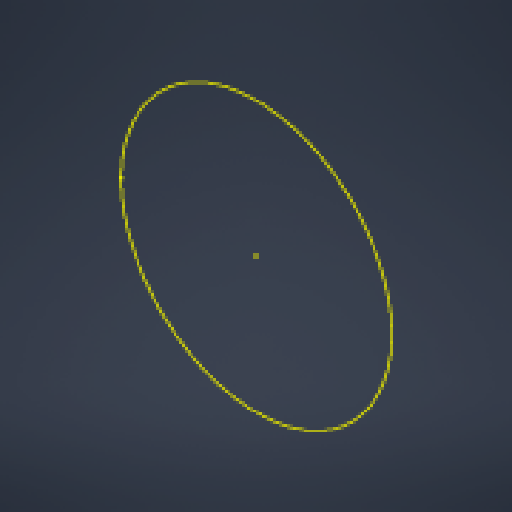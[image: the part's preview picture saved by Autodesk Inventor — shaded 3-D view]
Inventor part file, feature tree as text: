
AUTODESK INVENTOR PART (.ipt)
format: ipt  version: 2024.1 (Build 281209000, 209)  size: 106,496 bytes
history: native  units: in
note: dims shown in document units (in); Inventor stores cm internally (conversion verified against a paired STEP export)
features: other x3, sketch x1, reference x1
ambient origin geometry x8: Origin, YZ Plane, XZ Plane, XY Plane, X Axis, Y Axis, Z Axis, Center Point
feature tree (5):
  sketch  "Sketch1"
  reference  "Reference1"
  other  "<userpath>\Documents\School\FallCAD\Trebuchet\Trebuchet.iam"
  other  "Trebuchet.iam"
  other  "BallBearing_8x22x7mm:3"
